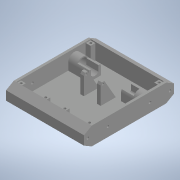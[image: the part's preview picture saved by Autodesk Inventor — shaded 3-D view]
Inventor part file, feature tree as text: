
AUTODESK INVENTOR PART (.ipt)
format: ipt  version: 2020 (Build 240168000, 168)  size: 400,384 bytes
history: native  units: in
note: dims shown in document units (in); Inventor stores cm internally (conversion verified against a paired STEP export)
features: projected_geometry x13, extrude x11, sketch x11, mirror x4, plane x1
ambient origin geometry x8: Origin, YZ Plane, XZ Plane, XY Plane, X Axis, Y Axis, Z Axis, Center Point
bodies: Solid1 (feature_tree)
feature tree (40):
  extrude  "Extrusion1"  Depth=5.9055in
  extrude  "Extrusion2"  TaperAngle=0.0deg  [1 undecoded]
  extrude  "Extrusion3"  Depth=1.063in
  extrude  "Extrusion4"  Depth=0.315in
  extrude  "Extrusion5"  TaperAngle=0.0deg  [1 undecoded]
  extrude  "Extrusion6"  Depth=0.5906in
  mirror  "Mirror1"
  extrude  "Extrusion7"  Depth=0.0787in
  mirror  "Mirror2"
  extrude  "Extrusion8"  Depth=0.5512in
  mirror  "Mirror3"
  plane  "Work Plane1"
  extrude  "Extrusion9"  Depth=0.7874in TaperAngle=0.0deg
  mirror  "Mirror4"
  extrude  "Extrusion10"  Depth=6.063in TaperAngle=0.0deg
  extrude  "Extrusion11"  Depth=0.1575in
  sketch  "Sketch1"  dims[d0=1.1811in d1=5.9055in]
  sketch  "Sketch2"  dims[d2=5.1181in d3=0.0in]
  projected_geometry  "Projected Loop1"
  sketch  "Sketch3"  dims[d4=0.1575in d5=1.063in]
  projected_geometry  "Projected Loop2"
  projected_geometry  "Projected Loop3"
  sketch  "Sketch4"  dims[d6=0.0in d8=0.315in]
  sketch  "Sketch5"  dims[d10=0.993in d11=0.0in]
  projected_geometry  "Projected Loop4"
  sketch  "Sketch6"  dims[d12=0.6496in d13=0.5906in]
  sketch  "Sketch7"  dims[d14=1.5748in d15=0.0787in]
  sketch  "Sketch9"  dims[d16=0.5512in d17=0.0in d18=0.6102in]
  sketch  "Sketch10"  dims[d19=0.4803in d20=0.7874in d21=0.0in]
  sketch  "Sketch12"  dims[d22=0.1654in d23=6.063in d24=0.0in]
  projected_geometry  "Projected Loop6"
  projected_geometry  "Projected Loop7"
  projected_geometry  "Projected Loop8"
  sketch  "Sketch13"  dims[d25=0.5114in d26=0.1575in d27=1.5748in d28=0.0in d29=0.0in d30=0.1575in d31=0.2756in d32=0.0in d33=0.4331in d34=0.122in d38=2.7559in d40=0.061in d41=0.0909in d42=0.2362in d43=0.0in d44=60.0deg d45=0.0787in d46=0.315in d48=0.993in d49=0.0in d51=0.1575in d52=0.1575in d53=0.2756in d54=0.0in d55=0.4724in]
  projected_geometry  "Projected Loop9"
  projected_geometry  "Projected Loop10"
  projected_geometry  "Projected Loop11"
  projected_geometry  "Projected Loop12"
  projected_geometry  "Projected Loop13"
  projected_geometry  "Projected Loop14"
note: 2 required parameter values undecoded (feature->parameter linkage not recoverable at this tier; creation-order binding heuristic only, values carry confidence <= 0.55)
